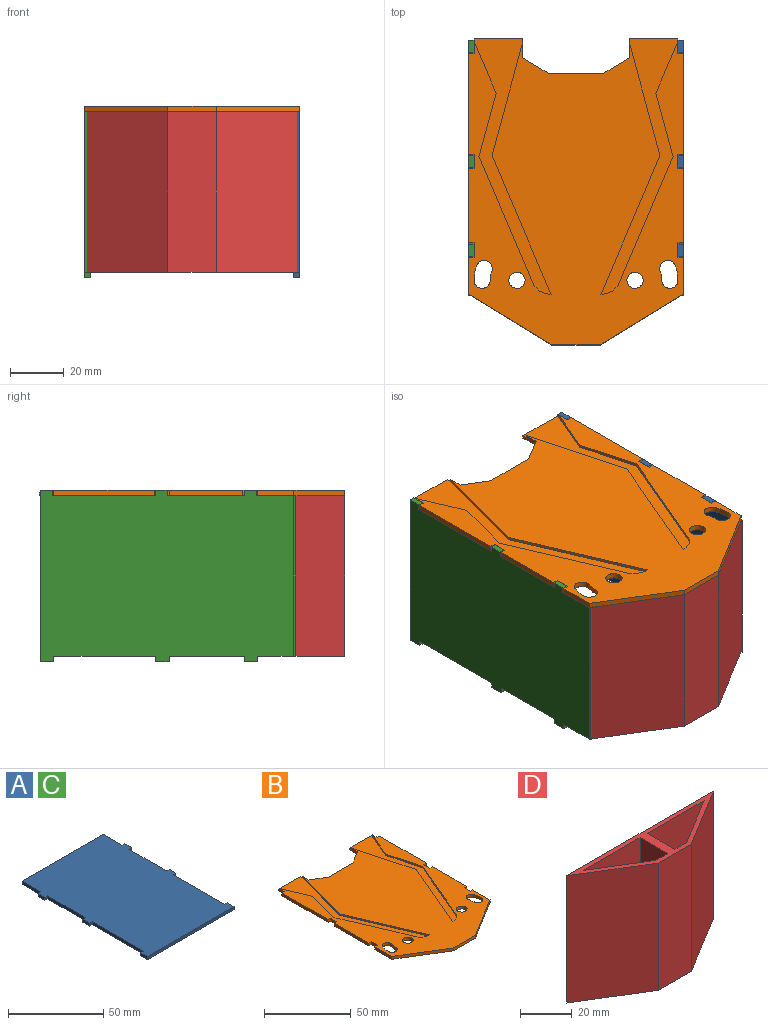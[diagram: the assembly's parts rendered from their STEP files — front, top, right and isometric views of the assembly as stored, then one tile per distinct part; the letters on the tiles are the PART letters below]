
ASSEMBLY  parts=4 mates=3
PART A: 26 faces, bbox 64x95x2 mm
  f0: plane 64x2mm, normal (0,-1,0), area 128mm2, adj f1,f23,f24,f25
  f1: plane 5x2mm, normal (1,0,0), area 10mm2, adj f0,f2,f24,f25
  f2: plane 2x2mm, normal (0,1,0), area 4mm2, adj f1,f3,f24,f25
  f3: plane 38x2mm, normal (1,0,0), area 76mm2, adj f2,f4,f24,f25
  f4: plane 2x2mm, normal (0,-1,0), area 4mm2, adj f3,f5,f24,f25
  f5: plane 5x2mm, normal (1,0,0), area 10mm2, adj f4,f6,f24,f25
  f6: plane 2x2mm, normal (0,1,0), area 4mm2, adj f5,f7,f24,f25
  f7: plane 28x2mm, normal (1,0,0), area 56mm2, adj f6,f8,f24,f25
  f8: plane 2x2mm, normal (0,-1,0), area 4mm2, adj f7,f9,f24,f25
  f9: plane 5x2mm, normal (1,0,0), area 10mm2, adj f8,f10,f24,f25
  f10: plane 2x2mm, normal (0,1,0), area 4mm2, adj f9,f11,f24,f25
  f11: plane 14x2mm, normal (1,0,0), area 28mm2, adj f10,f12,f24,f25
  f12: plane 60x2mm, normal (0,1,0), area 120mm2, adj f11,f13,f24,f25
  f13: plane 14x2mm, normal (-1,0,0), area 28mm2, adj f12,f14,f24,f25
  f14: plane 2x2mm, normal (0,1,0), area 4mm2, adj f13,f15,f24,f25
  f15: plane 5x2mm, normal (-1,0,0), area 10mm2, adj f14,f16,f24,f25
  f16: plane 2x2mm, normal (0,-1,0), area 4mm2, adj f15,f17,f24,f25
  f17: plane 28x2mm, normal (-1,0,0), area 56mm2, adj f16,f18,f24,f25
  f18: plane 2x2mm, normal (0,1,0), area 4mm2, adj f17,f19,f24,f25
  f19: plane 5x2mm, normal (-1,0,0), area 10mm2, adj f18,f20,f24,f25
  f20: plane 2x2mm, normal (0,-1,0), area 4mm2, adj f19,f21,f24,f25
  f21: plane 38x2mm, normal (-1,0,0), area 76mm2, adj f20,f22,f24,f25
  f22: plane 2x2mm, normal (0,1,0), area 4mm2, adj f21,f23,f24,f25
  f23: plane 5x2mm, normal (-1,0,0), area 10mm2, adj f0,f22,f24,f25
  f24: plane 95x64mm, normal (0,0,1), area 5760mm2, adj f0,f1,f2,f3,f4,f5,f6,f7
  f25: plane 95x64mm, normal (0,0,-1), area 5760mm2, adj f0,f1,f2,f3,f4,f5,f6,f7
PART B: 64 faces, bbox 80x114x2 mm
  f0: plane 14x2mm, normal (1,0,0), area 28mm2, adj f3,f4,f9,f31
  f1: plane 38x2mm, normal (1,0,0), area 76mm2, adj f3,f4,f26,f28
  f2: plane 28x2mm, normal (1,0,0), area 56mm2, adj f3,f4,f29,f33
  f3: plane 113.06x80mm, normal (0,0,1), area 6633.8mm2, adj f0,f1,f2,f5,f7,f8,f9,f11
  f4: plane 114x80mm, normal (0,0,-1), area 7843.4mm2, adj f0,f1,f2,f7,f8,f9,f10,f11
  f5: plane 19.27x8.23mm, normal (-0.92,0.39,0), area 21mm2, adj f3,f6,f18,f27
  f6: plane 95.18x28.72mm, normal (0,0,1), area 604.8mm2, adj f5,f7,f10,f18,f19,f20,f21,f22
  f7: plane 7x2mm, normal (-1,0,0), area 12.2mm2, adj f3,f4,f6,f10,f11,f19
  f8: plane 18x2mm, normal (0,-1,0), area 36mm2, adj f3,f4,f9,f40
  f9: plane 31x19mm, normal (0.52,-0.85,0), area 72.7mm2, adj f0,f3,f4,f8
  f10: plane 18x1mm, normal (0,1,0), area 18mm2, adj f4,f6,f7,f27
  f11: plane 10x6mm, normal (-0.51,0.86,0), area 23.3mm2, adj f3,f4,f7,f15
  f12: cylinder r=16mm len=5.47mm, axis (0,0,-1), area 11.2mm2, adj f3,f4,f13,f16
  f13: cylinder r=3mm len=6mm, axis (0,0,-1), area 18.8mm2, adj f3,f4,f12,f14
  f14: cylinder r=10mm len=3.42mm, axis (0,0,-1), area 7mm2, adj f3,f4,f13,f16
  f15: plane 20x2mm, normal (0,1,0), area 40mm2, adj f3,f4,f11,f42
  f16: cylinder r=3mm len=5.82mm, axis (0,0,-1), area 18.8mm2, adj f3,f4,f12,f14
  f17: cylinder r=3mm len=6mm, axis (0,0,-1), area 37.7mm2, adj f3,f4
  f18: plane 23.61x6.4mm, normal (-0.97,-0.26,0), area 24.5mm2, adj f3,f5,f6,f25
  f19: plane 41.69x11.3mm, normal (0.97,0.26,0), area 43.2mm2, adj f3,f6,f7,f20
  f20: plane 51.72x22.02mm, normal (0.92,-0.39,0), area 56.2mm2, adj f3,f6,f19,f21
  f21: plane 1.72x1mm, normal (-0.1,0.99,0), area 1.7mm2, adj f3,f6,f20,f22
  f22: plane 2.7x1mm, normal (-0.35,0.94,0), area 2.9mm2, adj f3,f6,f21,f23
  f23: plane 2x2mm, normal (-0.71,0.71,0), area 2.8mm2, adj f3,f6,f22,f24
  f24: plane 3.75x1.55mm, normal (-0.92,0.38,0), area 4.1mm2, adj f3,f6,f23,f25
  f25: plane 44.43x18.92mm, normal (-0.92,0.39,0), area 48.3mm2, adj f3,f6,f18,f24
  f26: plane 2x2mm, normal (0,1,0), area 4mm2, adj f1,f3,f4,f27
  f27: plane 5x2mm, normal (1,0,0), area 9.1mm2, adj f3,f4,f5,f6,f10,f26
  f28: plane 2x2mm, normal (0,-1,0), area 4mm2, adj f1,f3,f4,f30
  f29: plane 2x2mm, normal (0,1,0), area 4mm2, adj f2,f3,f4,f30
  f30: plane 5x2mm, normal (1,0,0), area 10mm2, adj f3,f4,f28,f29
  f31: plane 2x2mm, normal (0,1,0), area 4mm2, adj f0,f3,f4,f32
  f32: plane 5x2mm, normal (1,0,0), area 10mm2, adj f3,f4,f31,f33
  f33: plane 2x2mm, normal (0,-1,0), area 4mm2, adj f2,f3,f4,f32
  f34: plane 14x2mm, normal (-1,0,0), area 28mm2, adj f3,f4,f40,f61
  f35: plane 38x2mm, normal (-1,0,0), area 76mm2, adj f3,f4,f56,f58
  f36: plane 28x2mm, normal (-1,0,0), area 56mm2, adj f3,f4,f59,f63
  f37: plane 19.27x8.23mm, normal (0.92,0.39,0), area 21mm2, adj f3,f38,f48,f57
  f38: plane 95.18x28.72mm, normal (0,0,1), area 604.8mm2, adj f37,f39,f41,f48,f49,f50,f51,f52
  f39: plane 7x2mm, normal (1,0,0), area 12.2mm2, adj f3,f4,f38,f41,f42,f49
  f40: plane 31x19mm, normal (-0.52,-0.85,0), area 72.7mm2, adj f3,f4,f8,f34
  f41: plane 18x1mm, normal (0,1,0), area 18mm2, adj f4,f38,f39,f57
  f42: plane 10x6mm, normal (0.51,0.86,0), area 23.3mm2, adj f3,f4,f15,f39
  f43: cylinder r=16mm len=5.47mm, axis (0,0,-1), area 11.2mm2, adj f3,f4,f44,f46
  f44: cylinder r=3mm len=6mm, axis (0,0,-1), area 18.8mm2, adj f3,f4,f43,f45
  f45: cylinder r=10mm len=3.42mm, axis (0,0,-1), area 7mm2, adj f3,f4,f44,f46
  f46: cylinder r=3mm len=5.82mm, axis (0,0,-1), area 18.8mm2, adj f3,f4,f43,f45
  f47: cylinder r=3mm len=6mm, axis (0,0,-1), area 37.7mm2, adj f3,f4
  f48: plane 23.61x6.4mm, normal (0.97,-0.26,0), area 24.5mm2, adj f3,f37,f38,f55
  f49: plane 41.69x11.3mm, normal (-0.97,0.26,0), area 43.2mm2, adj f3,f38,f39,f50
  f50: plane 51.72x22.02mm, normal (-0.92,-0.39,0), area 56.2mm2, adj f3,f38,f49,f51
  f51: plane 1.72x1mm, normal (0.1,0.99,0), area 1.7mm2, adj f3,f38,f50,f52
  f52: plane 2.7x1mm, normal (0.35,0.94,0), area 2.9mm2, adj f3,f38,f51,f53
  f53: plane 2x2mm, normal (0.71,0.71,0), area 2.8mm2, adj f3,f38,f52,f54
  f54: plane 3.75x1.55mm, normal (0.92,0.38,0), area 4.1mm2, adj f3,f38,f53,f55
  f55: plane 44.43x18.92mm, normal (0.92,0.39,0), area 48.3mm2, adj f3,f38,f48,f54
  f56: plane 2x2mm, normal (0,1,0), area 4mm2, adj f3,f4,f35,f57
  f57: plane 5x2mm, normal (-1,0,0), area 9.1mm2, adj f3,f4,f37,f38,f41,f56
  f58: plane 2x2mm, normal (0,-1,0), area 4mm2, adj f3,f4,f35,f60
  f59: plane 2x2mm, normal (0,1,0), area 4mm2, adj f3,f4,f36,f60
  f60: plane 5x2mm, normal (-1,0,0), area 10mm2, adj f3,f4,f58,f59
  f61: plane 2x2mm, normal (0,1,0), area 4mm2, adj f3,f4,f34,f62
  f62: plane 5x2mm, normal (-1,0,0), area 10mm2, adj f3,f4,f61,f63
  f63: plane 2x2mm, normal (0,-1,0), area 4mm2, adj f3,f4,f36,f62
PART C: same geometry as A
PART D: 14 faces, bbox 80x19x60 mm
  f0: plane 60x15mm, normal (1,0,0), area 900mm2, adj f1,f6,f7,f8
  f1: plane 60x30.91mm, normal (0,-1,0), area 1854.6mm2, adj f0,f2,f7,f8
  f2: plane 60x24.47mm, normal (-0.52,0.85,0), area 1722.3mm2, adj f1,f6,f7,f8
  f3: plane 80x60mm, normal (0,1,0), area 4800mm2, adj f5,f7,f8,f12
  f4: plane 60x18mm, normal (0,-1,0), area 1080mm2, adj f5,f7,f8,f12
  f5: plane 60x31mm, normal (0.52,-0.85,0), area 2181.6mm2, adj f3,f4,f7,f8
  f6: plane 60x6.44mm, normal (0,1,0), area 386.2mm2, adj f0,f2,f7,f8
  f7: plane 80x19mm, normal (0,0,1), area 370.8mm2, adj f0,f1,f2,f3,f4,f5,f6,f9
  f8: plane 80x19mm, normal (0,0,-1), area 370.8mm2, adj f0,f1,f2,f3,f4,f5,f6,f9
  f9: plane 60x15mm, normal (-1,0,0), area 900mm2, adj f7,f8,f10,f13
  f10: plane 60x30.91mm, normal (0,-1,0), area 1854.6mm2, adj f7,f8,f9,f11
  f11: plane 60x24.47mm, normal (0.52,0.85,0), area 1722.3mm2, adj f7,f8,f10,f13
  f12: plane 60x31mm, normal (-0.52,-0.85,0), area 2181.6mm2, adj f3,f4,f7,f8
  f13: plane 60x6.44mm, normal (0,1,0), area 386.2mm2, adj f7,f8,f9,f11
PLACE A rot(axis=(0.71,0,0.71),180deg) t=(38,5.16,-23.44)mm
PLACE B t=(0,10.63,0)mm
PLACE C rot(axis=(0.71,0,0.71),180deg) t=(-40,5.16,-23.44)mm
PLACE D t=(0,10.63,-60)mm
MATE fastened C.f24 <-> B.f57  axis (1,0,0) through (-38,52.66,2)mm
MATE fastened A.f25 <-> B.f27  axis (-1,0,0) through (38,52.66,2)mm
MATE fastened D.f7 <-> B.f4  axis (0,0,1) through (0,-58.37,0)mm
